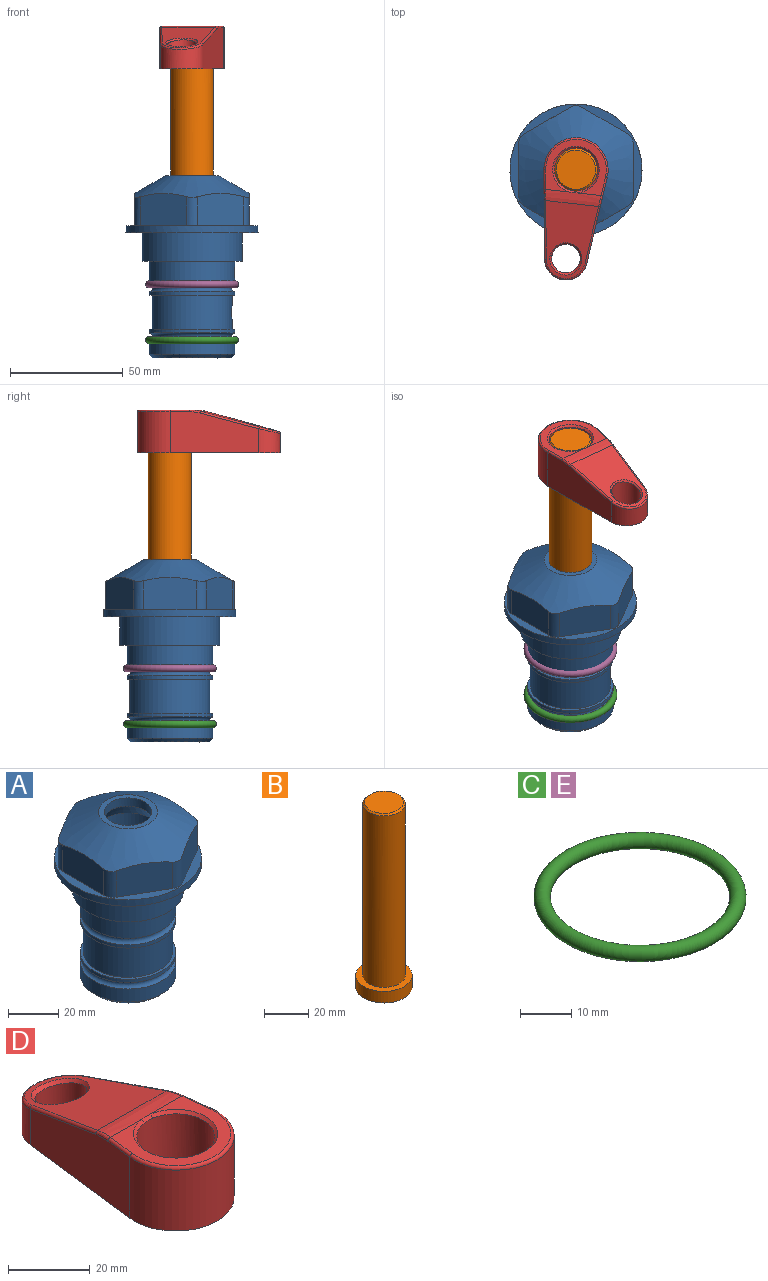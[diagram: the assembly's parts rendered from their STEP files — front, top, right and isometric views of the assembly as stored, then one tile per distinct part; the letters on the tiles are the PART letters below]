
ASSEMBLY  parts=5 mates=4
PART A: 36 faces, bbox 58.7x58.7x81 mm
  f0: cylinder r=17.78mm len=35.56mm, axis (0,0,1), area 1670.8mm2, adj f23,f24,f31
  f1: cylinder r=19.05mm len=38.1mm, axis (0,0,1), area 1191.9mm2, adj f26,f27,f30
  f2: plane 58.66x58.66mm, normal (0,0,-1), area 1150.6mm2, adj f3,f28
  f3: cylinder r=29.33mm len=58.66mm, axis (0,0,-1), area 585.1mm2, adj f2,f4
  f4: plane 58.66x58.66mm, normal (0,0,1), area 475.9mm2, adj f3,f5,f6,f7,f8,f9,f10,f11
  f5: plane 20.32x14.34mm, normal (-0.5,0.87,0), area 324.4mm2, adj f4,f15,f16,f17
  f6: plane 20.32x14.34mm, normal (0.5,0.87,0), area 324.4mm2, adj f4,f14,f15,f17
  f7: plane 23.48x14.34mm, normal (1,0,0), area 324.4mm2, adj f4,f13,f14,f17
  f8: plane 20.32x14.34mm, normal (0.5,-0.87,0), area 324.4mm2, adj f4,f12,f13,f17
  f9: plane 20.32x14.34mm, normal (-0.5,-0.87,0), area 324.4mm2, adj f4,f11,f12,f17
  f10: plane 23.48x14.34mm, normal (-1,0,0), area 324.4mm2, adj f4,f11,f16,f17
  f11: cylinder r=5.08mm len=12.85mm, axis (0,0,-1), area 67.2mm2, adj f4,f9,f10,f17
  f12: cylinder r=5.08mm len=12.85mm, axis (0,0,-1), area 67.2mm2, adj f4,f8,f9,f17
  f13: cylinder r=5.08mm len=12.85mm, axis (0,0,-1), area 67.2mm2, adj f4,f7,f8,f17
  f14: cylinder r=5.08mm len=12.85mm, axis (0,0,-1), area 67.2mm2, adj f4,f6,f7,f17
  f15: cylinder r=5.08mm len=12.85mm, axis (0,0,-1), area 67.2mm2, adj f4,f5,f6,f17
  f16: cylinder r=5.08mm len=12.85mm, axis (0,0,-1), area 67.2mm2, adj f4,f5,f10,f17
  f17: cone r=11.73mm half-angle=60deg, axis (0,0,-1), area 2071.8mm2, adj f5,f6,f7,f8,f9,f10,f11,f12
  f18: plane 23.46x23.46mm, normal (0,0,1), area 147.4mm2, adj f17,f35
  f19: plane 34.93x34.93mm, normal (0,0,-1), area 958mm2, adj f29
  f20: cylinder r=19.05mm len=38.1mm, axis (0,0,1), area 760.1mm2, adj f21,f29
  f21: torus R=19.05mm, axis (0,0,1), area 565.3mm2, adj f20,f22
  f22: cylinder r=19.05mm len=38.1mm, axis (0,0,1), area 190mm2, adj f21,f23
  f23: plane 38.1x38.1mm, normal (0,0,1), area 146.9mm2, adj f0,f22
  f24: plane 38.1x38.1mm, normal (0,0,-1), area 146.9mm2, adj f0,f25
  f25: cylinder r=19.05mm len=38.1mm, axis (0,0,1), area 190mm2, adj f24,f26
  f26: torus R=19.05mm, axis (0,0,1), area 565.3mm2, adj f1,f25
  f27: plane 44.45x44.45mm, normal (0,0,-1), area 411.7mm2, adj f1,f28
  f28: cylinder r=22.23mm len=44.45mm, axis (0,0,1), area 1773.5mm2, adj f2,f27
  f29: cone r=19.05mm half-angle=45deg, axis (0,0,1), area 257.5mm2, adj f19,f20
  f30: cylinder r=3.17mm len=6.75mm, axis (-1,0,0), area 128mm2, adj f1,f33
  f31: cylinder r=3.17mm len=6.35mm, axis (-1,0,0), area 102.5mm2, adj f0,f33
  f32: plane 25.4x25.4mm, normal (0,0,1), area 506.7mm2, adj f33
  f33: cylinder r=12.7mm len=66.42mm, axis (0,0,-1), area 5236.2mm2, adj f30,f31,f32,f34
  f34: cone r=9.53mm half-angle=30deg, axis (0,0,-1), area 443.4mm2, adj f33,f35
  f35: cylinder r=9.53mm len=19.05mm, axis (0,0,-1), area 240.9mm2, adj f18,f34
PART B: 6 faces, bbox 25.4x25.4x101.6 mm
  f0: plane 17.46x17.46mm, normal (0,0,1), area 239.5mm2, adj f5
  f1: plane 25.4x25.4mm, normal (0,0,-1), area 506.7mm2, adj f2
  f2: cylinder r=12.7mm len=25.4mm, axis (0,0,1), area 506.7mm2, adj f1,f3
  f3: plane 25.4x25.4mm, normal (0,0,1), area 221.7mm2, adj f2,f4
  f4: cylinder r=9.53mm len=94.46mm, axis (0,0,1), area 5653mm2, adj f3,f5
  f5: cone r=8.73mm half-angle=45deg, axis (0,0,-1), area 64.4mm2, adj f0,f4
PART C: 1 faces, bbox 44.7x44.7x3.2 mm
  f0: torus R=19.05mm, axis (0,0,1), area 1193.9mm2
PART D: 31 faces, bbox 31.7x65.5x19.8 mm
  f0: plane 39.12x18.26mm, normal (0.99,0.12,0), area 612.2mm2, adj f1,f4,f7,f11,f13,f15
  f1: cylinder r=9.53mm len=18.91mm, axis (0,0,-1), area 296.1mm2, adj f0,f2,f7,f17
  f2: plane 39.12x18.26mm, normal (-0.99,0.12,0), area 612.2mm2, adj f1,f4,f7,f12,f14,f16
  f3: cylinder r=6.35mm len=12.7mm, axis (0,0,-1), area 362.4mm2, adj f7,f18
  f4: cylinder r=14.29mm len=28.58mm, axis (0,0,-1), area 882.2mm2, adj f0,f2,f7,f10
  f5: cylinder r=9.53mm len=19.05mm, axis (0,0,-1), area 1092.6mm2, adj f7,f19,f20
  f6: plane 26.99x23.69mm, normal (0,0,1), area 216.2mm2, adj f9,f10,f11,f12,f19
  f7: plane 63.5x28.58mm, normal (0,0,-1), area 661.8mm2, adj f0,f1,f2,f3,f4,f5,f22,f23
  f8: plane 33.52x23.6mm, normal (0,0.26,0.97), area 486mm2, adj f9,f15,f16,f17,f18
  f9: cylinder r=19.05mm len=24.72mm, axis (1,0,0), area 120.4mm2, adj f6,f8,f13,f14,f20
  f10: torus R=13.49mm, axis (0,0,1), area 59mm2, adj f4,f6,f11,f12
  f11: cylinder r=0.79mm len=8.67mm, axis (0.12,-0.99,0), area 10.8mm2, adj f0,f6,f10,f13
  f12: cylinder r=0.79mm len=8.67mm, axis (0.12,0.99,0), area 10.8mm2, adj f2,f6,f10,f14
  f13: bspline ~4.95x1.42mm, area 6.1mm2, adj f0,f9,f11,f15
  f14: bspline ~4.95x1.42mm, area 6.1mm2, adj f2,f9,f12,f16
  f15: cylinder r=0.79mm len=25.95mm, axis (0.12,-0.96,0.26), area 32.9mm2, adj f0,f8,f13,f17
  f16: cylinder r=0.79mm len=25.95mm, axis (0.12,0.96,-0.26), area 32.9mm2, adj f2,f8,f14,f17
  f17: bspline ~18.91x8.38mm, area 30mm2, adj f1,f8,f15,f16
  f18: bspline ~14.29x14.29mm, area 48.3mm2, adj f3,f8
  f19: cone r=9.53mm half-angle=45deg, axis (0,0,1), area 66.5mm2, adj f5,f6,f20
  f20: bspline ~3.22x0.96mm, area 3.5mm2, adj f5,f9,f19
  f21: plane 2.75x2.72mm, normal (0,0,-1), area 2.9mm2, adj f23,f25,f28
  f22: plane 23.05x15.88mm, normal (-0.99,-0.12,0), area 323.6mm2, adj f7,f25,f26,f27,f28,f29
  f23: plane 23.05x15.88mm, normal (0.99,-0.12,0), area 323.6mm2, adj f7,f21,f25,f27,f28,f30
  f24: cylinder r=9.53mm len=10.69mm, axis (0,0,-1), area 114.7mm2, adj f7,f27,f29,f30
  f25: cylinder r=12.7mm len=20.59mm, axis (0,0,-1), area 381.1mm2, adj f7,f21,f22,f23,f26,f28
  f26: plane 2.75x2.72mm, normal (0,0,-1), area 2.9mm2, adj f22,f25,f28
  f27: plane 19.72x18.37mm, normal (0,-0.26,-0.97), area 291.8mm2, adj f22,f23,f24,f28,f29,f30
  f28: cylinder r=15.88mm len=19.92mm, axis (1,0,0), area 54.8mm2, adj f21,f22,f23,f25,f26,f27
  f29: cylinder r=1.59mm len=11mm, axis (0,0,-1), area 34.7mm2, adj f7,f22,f24,f27
  f30: cylinder r=1.59mm len=11mm, axis (0,0,-1), area 34.7mm2, adj f7,f23,f24,f27
PART E: same geometry as C
PLACE A t=(2.78,-4.77,3.26)mm
PLACE B rot(axis=(0,0,1),173.6deg) t=(2.78,-4.77,30.81)mm
PLACE C t=(2.78,-4.77,-19.92)mm
PLACE D rot(axis=(0,0,1),173.6deg) t=(2.78,-4.77,31.61)mm
PLACE E t=(2.78,-4.77,4.85)mm
MATE fastened B.f2 <-> D.f4  axis (0,0,1) through (2.78,-4.77,94.31)mm
MATE fastened C.f0 <-> A.f0  axis (0,0,1) through (2.78,-4.77,-44.43)mm
MATE cylindrical A.f0 <-> B.f2  axis (0,0,1) through (2.78,-4.77,-47.29)mm
MATE fastened A.f0 <-> E.f0  axis (0,0,1) through (2.78,-4.77,-19.67)mm
